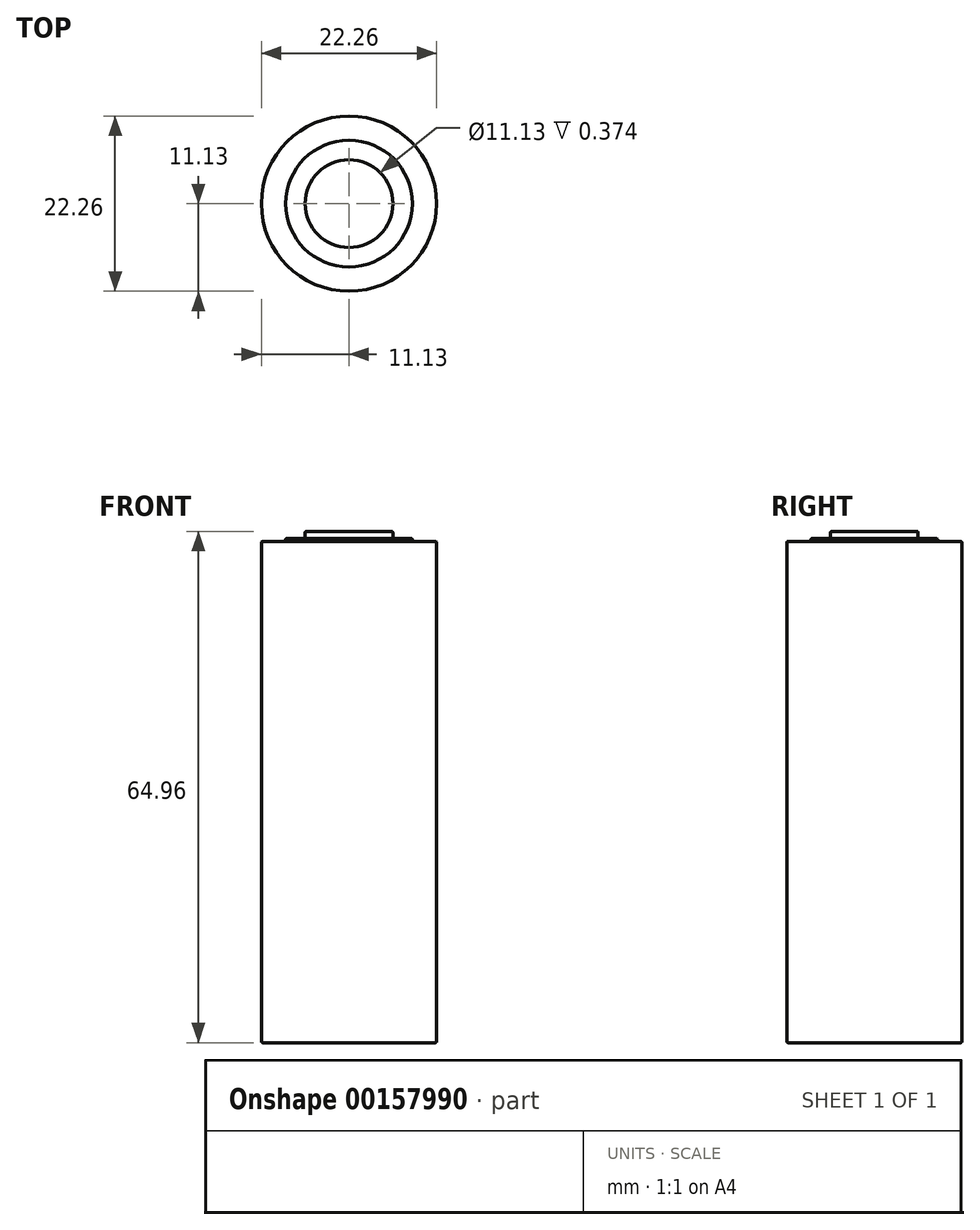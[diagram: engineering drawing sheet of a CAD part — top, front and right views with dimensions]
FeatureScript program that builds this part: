
annotation { "Feature Type Name" : "Feature", "Feature Type Description" : "" }
export const myFeature = defineFeature(function(context is Context, id is Id, definition is map)
    precondition{}
    {
        {
            var Q0;
            Q0=qCreatedBy(makeId("Front.planeOp"),FACE);
            var sketch = newSketch(context, id + "F0", { "sketchPlane" : qUnion([Q0])});
            skLineSegment(sketch, "E0.bottom", {"start": v(0, 0) * mm, "end": v(10.95, 0) * mm});
            skLineSegment(sketch, "E0.top", {"start": v(0, 63.69) * mm, "end": v(10.95, 63.69) * mm});
            skLineSegment(sketch, "E0.left", {"start": v(0, 0) * mm, "end": v(0, 63.69) * mm});
            skLineSegment(sketch, "E0.right", {"start": v(11.13, 0.18) * mm, "end": v(11.13, 63.5) * mm});
            skPoint(sketch, "E1.oppositeSnap0", {"position": v(5.57, 63.69) * mm});
            skLineSegment(sketch, "E1.bottom", {"start": v(0, 63.69) * mm, "end": v(5.57, 63.69) * mm});
            skLineSegment(sketch, "E1.top", {"start": v(0, 64.96) * mm, "end": v(5.39, 64.96) * mm});
            skLineSegment(sketch, "E1.left", {"start": v(0, 63.69) * mm, "end": v(0, 64.96) * mm});
            skLineSegment(sketch, "E1.right", {"start": v(5.57, 63.69) * mm, "end": v(5.57, 64.78) * mm});
            skLineSegment(sketch, "E2.bottom", {"start": v(0, 0) * mm, "end": v(9.8, 0) * mm});
            skLineSegment(sketch, "E2.top", {"start": v(0, -0.37) * mm, "end": v(9.63, -0.37) * mm});
            skLineSegment(sketch, "E2.left", {"start": v(0, 0) * mm, "end": v(0, -0.37) * mm});
            skLineSegment(sketch, "E2.right", {"start": v(9.8, 0) * mm, "end": v(9.8, -0.18) * mm});
            skLineSegment(sketch, "E3.bottom", {"start": v(0, 63.69) * mm, "end": v(8.05, 63.69) * mm});
            skLineSegment(sketch, "E3.top", {"start": v(0, 64.06) * mm, "end": v(7.87, 64.06) * mm});
            skLineSegment(sketch, "E3.left", {"start": v(0, 63.69) * mm, "end": v(0, 64.06) * mm});
            skLineSegment(sketch, "E3.right", {"start": v(8.05, 63.69) * mm, "end": v(8.05, 63.88) * mm});
            skPoint(sketch, "E4.visualSharp", {"position": v(5.57, 64.96) * mm});
            skArc(sketch, "E4.filletArc", {"start": v(5.57, 64.78) * mm, "mid": v(5.51, 64.9) * mm, "end": v(5.39, 64.96) * mm});
            skPoint(sketch, "E5.visualSharp", {"position": v(8.05, 64.06) * mm});
            skArc(sketch, "E5.filletArc", {"start": v(8.05, 63.88) * mm, "mid": v(8, 64) * mm, "end": v(7.87, 64.06) * mm});
            skPoint(sketch, "E6.visualSharp", {"position": v(11.13, 63.69) * mm});
            skArc(sketch, "E6.filletArc", {"start": v(11.13, 63.5) * mm, "mid": v(11.08, 63.63) * mm, "end": v(10.95, 63.69) * mm});
            skPoint(sketch, "E7.visualSharp", {"position": v(11.13, 0) * mm});
            skArc(sketch, "E7.filletArc", {"start": v(10.95, 0) * mm, "mid": v(11.08, 0.05) * mm, "end": v(11.13, 0.18) * mm});
            skPoint(sketch, "E8.visualSharp", {"position": v(9.8, -0.37) * mm});
            skArc(sketch, "E8.filletArc", {"start": v(9.63, -0.37) * mm, "mid": v(9.76, -0.31) * mm, "end": v(9.8, -0.18) * mm});
            skSolve(sketch);
        }
        {
            var Q0;
            Q0=makeQuery(id+"F0.imprint","IMPRINT",FACE,{"disambiguationData":[TD([[makeQuery(id+"F0.imprint","IMPRINT",EDGE,{"derivedFrom":sQuery(id+"F0.wireOp",EDGE,"E1.top")}),-1.0]])]});
            var Q1;
            {var subQ5=sQuery(id+"F0.wireOp",EDGE,"E3.left");Q1=makeQuery(id+"F0.imprint","IMPRINT",FACE,{"disambiguationData":[TD([[makeQuery(id+"F0.imprint","IMPRINT",EDGE,{"derivedFrom":subQ5}),-1.0]])]});}
            var Q2;
            {var subQ0=sQuery(id+"F0.wireOp",EDGE,"E3.right");Q2=makeQuery(id+"F0.imprint","IMPRINT",FACE,{"disambiguationData":[TD([[makeQuery(id+"F0.imprint","IMPRINT",EDGE,{"derivedFrom":subQ0}),1.0]])]});}
            var Q3;
            Q3=makeQuery(id+"F0.imprint","IMPRINT",FACE,{"disambiguationData":[TD([[makeQuery(id+"F0.imprint","IMPRINT",EDGE,{"derivedFrom":sQuery(id+"F0.wireOp",EDGE,"E0.bottom")}),1.0]])]});
            var Q4;
            Q4=makeQuery(id+"F0.imprint","IMPRINT",FACE,{"disambiguationData":[TD([[makeQuery(id+"F0.imprint","IMPRINT",EDGE,{"derivedFrom":sQuery(id+"F0.wireOp",EDGE,"E2.bottom")}),-1.0]])]});
            var Q5;
            Q5=sQuery(id+"F0.wireOp",EDGE,"E0.left");
            revolve(context, id + "F1", {"entities" : qUnion([Q0, Q1, Q2, Q3, Q4]), "axis" : qUnion([Q5]), "revolveType" : RevolveType.FULL});
        }
    });
